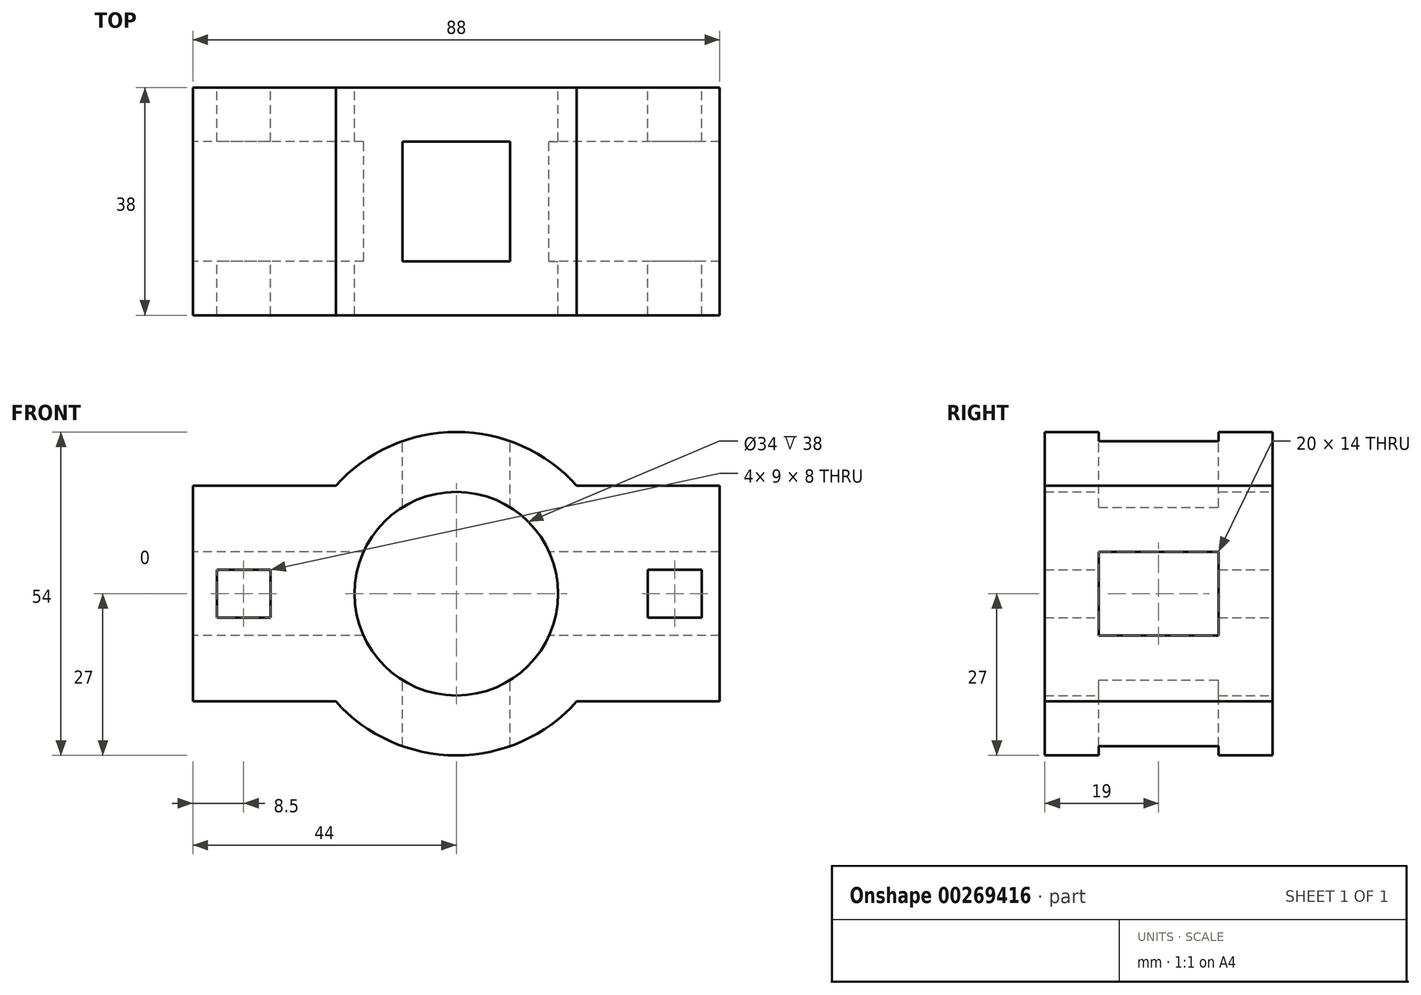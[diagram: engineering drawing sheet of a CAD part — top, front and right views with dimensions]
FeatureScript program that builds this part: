
annotation { "Feature Type Name" : "Feature", "Feature Type Description" : "" }
export const myFeature = defineFeature(function(context is Context, id is Id, definition is map)
    precondition{}
    {
        {
            var Q0;
            Q0=qCreatedBy(makeId("Front.planeOp"),FACE);
            var sketch = newSketch(context, id + "F0", { "sketchPlane" : qUnion([Q0])});
            skCircle(sketch, "E0", {"center": v(0, 0) * mm, "radius": 17 * mm});
            skCircle(sketch, "E1.0", {"center": v(0, 0) * mm, "radius": 27 * mm});
            skLineSegment(sketch, "E2.bottom", {"start": v(-44, -18) * mm, "end": v(44, -18) * mm});
            skLineSegment(sketch, "E2.top", {"start": v(-44, 18) * mm, "end": v(-20.12, 18) * mm});
            skLineSegment(sketch, "E2.left", {"start": v(-44, -18) * mm, "end": v(-44, 18) * mm});
            skLineSegment(sketch, "E2.right", {"start": v(44, -18) * mm, "end": v(44, 18) * mm});
            skLineSegment(sketch, "E3.bottom", {"start": v(-40, -4) * mm, "end": v(-31, -4) * mm});
            skLineSegment(sketch, "E3.top", {"start": v(-40, 4) * mm, "end": v(-31, 4) * mm});
            skLineSegment(sketch, "E3.left", {"start": v(-40, -4) * mm, "end": v(-40, 4) * mm});
            skLineSegment(sketch, "E3.right", {"start": v(-31, -4) * mm, "end": v(-31, 4) * mm});
            skLineSegment(sketch, "E4.bottom", {"start": v(32, -4) * mm, "end": v(41, -4) * mm});
            skLineSegment(sketch, "E4.top", {"start": v(32, 4) * mm, "end": v(41, 4) * mm});
            skLineSegment(sketch, "E4.left", {"start": v(32, -4) * mm, "end": v(32, 4) * mm});
            skLineSegment(sketch, "E4.right", {"start": v(41, -4) * mm, "end": v(41, 4) * mm});
            skLineSegment(sketch, "E5", {"start": v(-20.12, 18) * mm, "end": v(44, 18) * mm});
            skSolve(sketch);
        }
        {
            var Q0;
            {var subQ0=sQuery(id+"F0.wireOp",EDGE,"E2.left");Q0=makeQuery(id+"F0.imprint","IMPRINT",FACE,{"disambiguationData":[TD([[makeQuery(id+"F0.imprint","IMPRINT",EDGE,{"derivedFrom":subQ0}),-1.0]])]});}
            var Q1;
            Q1=makeQuery(id+"F0.imprint","IMPRINT",FACE,{"disambiguationData":[TD([[makeQuery(id+"F0.imprint","IMPRINT",EDGE,{"derivedFrom":sQuery(id+"F0.wireOp",EDGE,"E0")}),-1.0]])]});
            var Q2;
            {var subQ0=sQuery(id+"F0.wireOp",EDGE,"E2.top");var subQ1=sQuery(id+"F0.wireOp",EDGE,"E1.0");var subQ2=makeQuery(id+"F0.imprint","INTERSECT",VERTEX,{"disambiguationData":[OD(0.0)],"derivedFrom":[subQ1,subQ0]});Q2=makeQuery(id+"F0.imprint","IMPRINT",FACE,{"disambiguationData":[TD([[makeQuery(id+"F0.imprint","IMPRINT",EDGE,{"disambiguationData":[TD([[subQ2,1.0]])],"derivedFrom":subQ1}),1.0]])]});}
            var Q3;
            {var subQ0=sQuery(id+"F0.wireOp",EDGE,"E2.right");Q3=makeQuery(id+"F0.imprint","IMPRINT",FACE,{"disambiguationData":[TD([[makeQuery(id+"F0.imprint","IMPRINT",EDGE,{"derivedFrom":subQ0}),1.0]])]});}
            var Q4;
            {var subQ0=sQuery(id+"F0.wireOp",EDGE,"E2.bottom");var subQ1=sQuery(id+"F0.wireOp",EDGE,"E1.0");var subQ2=makeQuery(id+"F0.imprint","INTERSECT",VERTEX,{"disambiguationData":[OD(0.0)],"derivedFrom":[subQ1,subQ0]});Q4=makeQuery(id+"F0.imprint","IMPRINT",FACE,{"disambiguationData":[TD([[makeQuery(id+"F0.imprint","IMPRINT",EDGE,{"disambiguationData":[TD([[subQ2,-1.0]])],"derivedFrom":subQ1}),1.0]])]});}
            extrude(context, id + "F1", {"entities" : qUnion([Q0, Q1, Q2, Q3, Q4]), "depth" : 38 * mm});
        }
        {
            var Q0;
            Q0=makeQuery(id+"F1.opExtrude","SWEPT_FACE",FACE,{"disambiguationData":[OSD([sQuery(id+"F0.wireOp",EDGE,"E2.left")])]});
            var sketch = newSketch(context, id + "F2", { "sketchPlane" : qUnion([Q0])});
            skLineSegment(sketch, "E6.bottom", {"start": v(9, 7) * mm, "end": v(29, 7) * mm});
            skLineSegment(sketch, "E6.top", {"start": v(9, -7) * mm, "end": v(29, -7) * mm});
            skLineSegment(sketch, "E6.left", {"start": v(9, 7) * mm, "end": v(9, -7) * mm});
            skLineSegment(sketch, "E6.right", {"start": v(29, 7) * mm, "end": v(29, -7) * mm});
            skSolve(sketch);
        }
        {
            var Q0;
            Q0=makeQuery(id+"F2.imprint","IMPRINT",FACE,{"disambiguationData":[TD([[makeQuery(id+"F2.imprint","IMPRINT",EDGE,{"derivedFrom":sQuery(id+"F2.wireOp",EDGE,"E6.bottom")}),-1.0]])]});
            extrude(context, id + "F3", {"entities" : qUnion([Q0]), "operationType" : NewBodyOperationType.REMOVE, "oppositeDirection" : true, "depth" : 113.54 * mm});
        }
        {
            var Q0;
            {var subQ0=sQuery(id+"F0.wireOp",EDGE,"E2.top");Q0=makeQuery(id+"F1.opExtrude","SWEPT_FACE",FACE,{"disambiguationData":[OSD([subQ0]),TDD([makeQuery(id+"F0.imprint","IMPRINT",EDGE,{"disambiguationData":[TD([[makeQuery(id+"F0.imprint","INTERSECT",VERTEX,{"derivedFrom":[subQ0,sQuery(id+"F0.wireOp",EDGE,"E2.right")]}),1.0]])],"derivedFrom":subQ0})])]});}
            cPlane(context, id + "F4", {"entities" : qUnion([Q0]), "cplaneType" : CPlaneType.OFFSET, "offset" : 9 * mm, "width" : 152.4 * mm, "height" : 152.4 * mm});
        }
        {
            var Q0;
            Q0=qCreatedBy(id+"F4.planeOp",FACE);
            var sketch = newSketch(context, id + "F5", { "sketchPlane" : qUnion([Q0])});
            skLineSegment(sketch, "E7.bottom", {"start": v(-9, -9) * mm, "end": v(9, -9) * mm});
            skLineSegment(sketch, "E7.top", {"start": v(-9, -29) * mm, "end": v(9, -29) * mm});
            skLineSegment(sketch, "E7.left", {"start": v(-9, -9) * mm, "end": v(-9, -29) * mm});
            skLineSegment(sketch, "E7.right", {"start": v(9, -9) * mm, "end": v(9, -29) * mm});
            skSolve(sketch);
        }
        {
            var Q0;
            Q0=makeQuery(id+"F5.imprint","IMPRINT",FACE,{"disambiguationData":[TD([[makeQuery(id+"F5.imprint","IMPRINT",EDGE,{"derivedFrom":sQuery(id+"F5.wireOp",EDGE,"E7.bottom")}),-1.0]])]});
            extrude(context, id + "F6", {"entities" : qUnion([Q0]), "operationType" : NewBodyOperationType.REMOVE, "oppositeDirection" : true, "depth" : 71.63 * mm});
        }
    });
